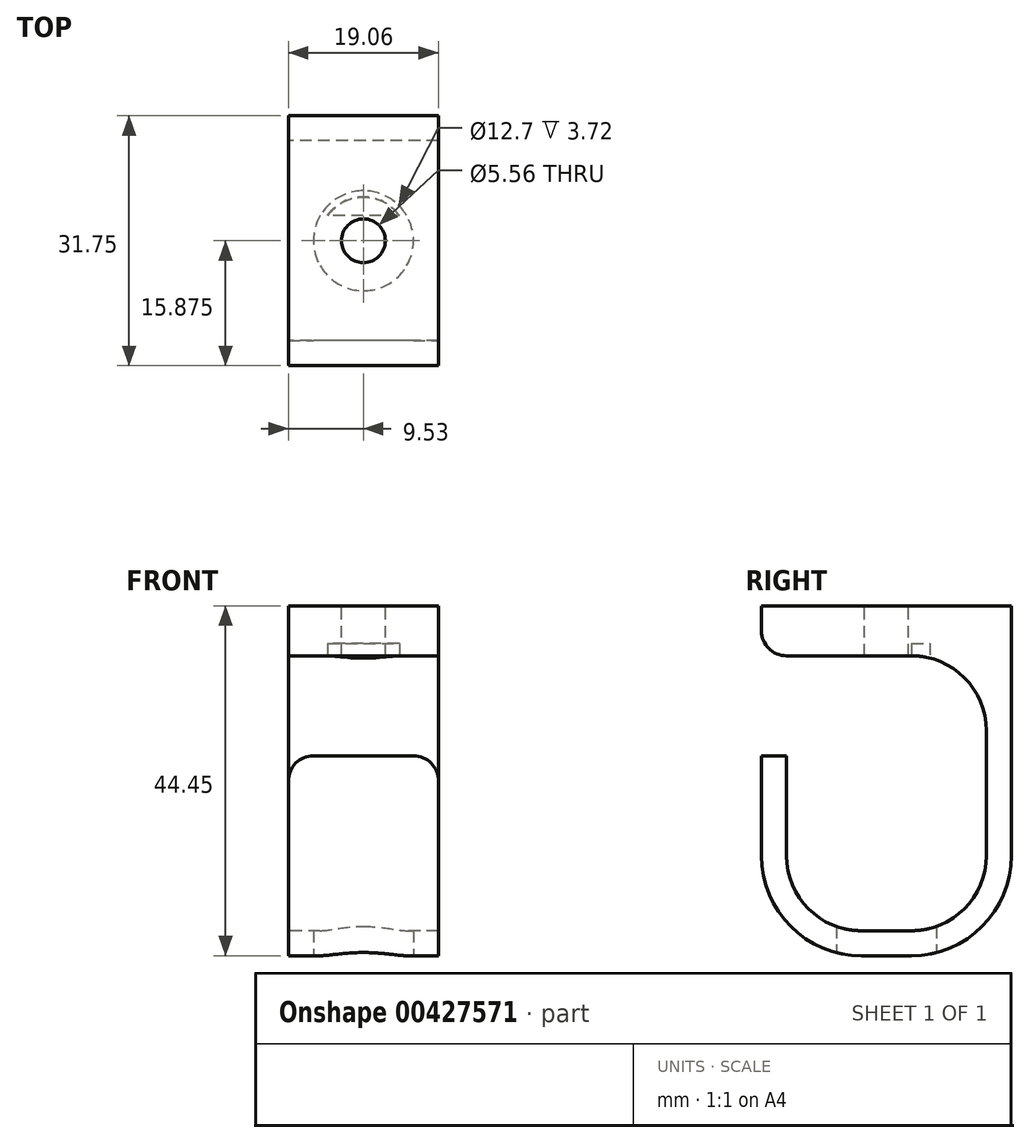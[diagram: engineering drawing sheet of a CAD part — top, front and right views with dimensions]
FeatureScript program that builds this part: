
annotation { "Feature Type Name" : "Feature", "Feature Type Description" : "" }
export const myFeature = defineFeature(function(context is Context, id is Id, definition is map)
    precondition{}
    {
        {
            var Q0;
            Q0=qCreatedBy(makeId("Right.planeOp"),FACE);
            var sketch = newSketch(context, id + "F0", { "sketchPlane" : qUnion([Q0])});
            skLineSegment(sketch, "E0.bottom", {"start": v(0, 44.45) * mm, "end": v(31.75, 44.45) * mm});
            skLineSegment(sketch, "E0.top", {"start": v(0, 0) * mm, "end": v(31.75, 0) * mm});
            skLineSegment(sketch, "E0.left", {"start": v(0, 44.45) * mm, "end": v(0, 0) * mm});
            skLineSegment(sketch, "E0.right", {"start": v(31.75, 44.45) * mm, "end": v(31.75, 0) * mm});
            skLineSegment(sketch, "E1", {"start": v(0, 38.1) * mm, "end": v(28.58, 38.1) * mm});
            skLineSegment(sketch, "E2", {"start": v(28.58, 38.1) * mm, "end": v(28.58, 0) * mm});
            skLineSegment(sketch, "E3", {"start": v(31.75, 3.18) * mm, "end": v(0, 3.17) * mm});
            skLineSegment(sketch, "E4", {"start": v(3.17, 44.45) * mm, "end": v(3.17, 0) * mm});
            skLineSegment(sketch, "E5", {"start": v(0, 12.7) * mm, "end": v(31.75, 12.7) * mm, "construction": true});
            skLineSegment(sketch, "E6", {"start": v(12.7, 0) * mm, "end": v(12.7, 44.45) * mm, "construction": true});
            skLineSegment(sketch, "E7", {"start": v(19.05, 44.45) * mm, "end": v(19.05, 0) * mm, "construction": true});
            skArc(sketch, "E8", {"start": v(3.17, 12.7) * mm, "mid": v(5.96, 5.96) * mm, "end": v(12.7, 3.17) * mm});
            skArc(sketch, "E9", {"start": v(19.05, 3.17) * mm, "mid": v(25.79, 5.96) * mm, "end": v(28.58, 12.7) * mm});
            skLineSegment(sketch, "E10", {"start": v(0, 28.57) * mm, "end": v(31.75, 28.58) * mm, "construction": true});
            skArc(sketch, "E11", {"start": v(28.58, 28.58) * mm, "mid": v(25.79, 35.31) * mm, "end": v(19.05, 38.1) * mm});
            skLineSegment(sketch, "E12", {"start": v(0, 25.4) * mm, "end": v(31.75, 25.4) * mm, "construction": true});
            skArc(sketch, "E13", {"start": v(0, 12.7) * mm, "mid": v(3.72, 3.72) * mm, "end": v(12.7, 0) * mm});
            skArc(sketch, "E14", {"start": v(19.05, 0) * mm, "mid": v(28.03, 3.72) * mm, "end": v(31.75, 12.7) * mm});
            skLineSegment(sketch, "E15", {"start": v(0, 25.4) * mm, "end": v(3.17, 25.4) * mm});
            skSolve(sketch);
        }
        {
            var Q0;
            {var subQ5=sQuery(id+"F0.wireOp",EDGE,"E0.right");var subQ6=sQuery(id+"F0.wireOp",EDGE,"E0.bottom");var subQ7=makeQuery(id+"F0.imprint","INTERSECT",VERTEX,{"derivedFrom":[subQ6,subQ5]});Q0=makeQuery(id+"F0.imprint","IMPRINT",FACE,{"disambiguationData":[TD([[makeQuery(id+"F0.imprint","IMPRINT",EDGE,{"disambiguationData":[TD([[subQ7,1.0]])],"derivedFrom":subQ6}),-1.0]])]});}
            var Q1;
            {var subQ0=sQuery(id+"F0.wireOp",EDGE,"E0.left");var subQ1=sQuery(id+"F0.wireOp",EDGE,"E0.bottom");var subQ2=makeQuery(id+"F0.imprint","INTERSECT",VERTEX,{"derivedFrom":[subQ1,subQ0]});Q1=makeQuery(id+"F0.imprint","IMPRINT",FACE,{"disambiguationData":[TD([[makeQuery(id+"F0.imprint","IMPRINT",EDGE,{"disambiguationData":[TD([[subQ2,-1.0]])],"derivedFrom":subQ1}),-1.0]])]});}
            var Q2;
            {var subQ3=sQuery(id+"F0.wireOp",EDGE,"E11");Q2=makeQuery(id+"F0.imprint","IMPRINT",FACE,{"disambiguationData":[TD([[makeQuery(id+"F0.imprint","IMPRINT",EDGE,{"derivedFrom":subQ3}),-1.0]])]});}
            var Q3;
            {var subQ0=sQuery(id+"F0.wireOp",EDGE,"E9");Q3=makeQuery(id+"F0.imprint","IMPRINT",FACE,{"disambiguationData":[TD([[makeQuery(id+"F0.imprint","IMPRINT",EDGE,{"derivedFrom":subQ0}),-1.0]])]});}
            var Q4;
            {var subQ2=sQuery(id+"F0.wireOp",EDGE,"E13");var subQ5=sQuery(id+"F0.wireOp",EDGE,"E0.top");var subQ6=makeQuery(id+"F0.imprint","INTERSECT",VERTEX,{"derivedFrom":[subQ5,subQ2]});Q4=makeQuery(id+"F0.imprint","IMPRINT",FACE,{"disambiguationData":[TD([[makeQuery(id+"F0.imprint","IMPRINT",EDGE,{"disambiguationData":[TD([[subQ6,-1.0]])],"derivedFrom":subQ5}),1.0]])]});}
            var Q5;
            {var subQ0=sQuery(id+"F0.wireOp",EDGE,"E8");Q5=makeQuery(id+"F0.imprint","IMPRINT",FACE,{"disambiguationData":[TD([[makeQuery(id+"F0.imprint","IMPRINT",EDGE,{"derivedFrom":subQ0}),-1.0]])]});}
            var Q6;
            {var subQ4=sQuery(id+"F0.wireOp",EDGE,"UCciuxyD-qlXf-moOq-a4FD-n2S9QXWjRClS");Q6=makeQuery(id+"F0.imprint","IMPRINT",FACE,{"disambiguationData":[TD([[makeQuery(id+"F0.imprint","IMPRINT",EDGE,{"derivedFrom":subQ4}),1.0]])]});}
            var Q7;
            {var subQ4=sQuery(id+"F0.wireOp",EDGE,"E15");Q7=makeQuery(id+"F0.imprint","IMPRINT",FACE,{"disambiguationData":[TD([[makeQuery(id+"F0.imprint","IMPRINT",EDGE,{"derivedFrom":subQ4}),-1.0]])]});}
            extrude(context, id + "F1", {"entities" : qUnion([Q0, Q1, Q2, Q3, Q4, Q5, Q6, Q7]), "endBound" : BoundingType.SYMMETRIC, "depth" : 19.05 * mm});
        }
        {
            var Q0;
            Q0=makeQuery(id+"F1.opExtrude","SWEPT_FACE",FACE,{"disambiguationData":[OSD([sQuery(id+"F0.wireOp",EDGE,"E0.top")])]});
            var sketch = newSketch(context, id + "F2", { "sketchPlane" : qUnion([Q0])});
            skLineSegment(sketch, "E16", {"start": v(0, -12.7) * mm, "end": v(0, -19.05) * mm, "construction": true});
            skLineSegment(sketch, "E17", {"start": v(9.53, -15.88) * mm, "end": v(-9.53, -15.88) * mm, "construction": true});
            skLineSegment(sketch, "E18.bottom", {"start": v(6.35, -22.23) * mm, "end": v(-6.35, -22.23) * mm});
            skLineSegment(sketch, "E18.top", {"start": v(6.35, -9.52) * mm, "end": v(-6.35, -9.52) * mm});
            skLineSegment(sketch, "E18.left", {"start": v(6.35, -22.23) * mm, "end": v(6.35, -9.53) * mm});
            skLineSegment(sketch, "E18.right", {"start": v(-6.35, -22.23) * mm, "end": v(-6.35, -9.53) * mm});
            skPoint(sketch, "E18.middle", {"position": v(0, -15.87) * mm});
            skSolve(sketch);
        }
        {
            var Q0;
            {var subQ0=sQuery(id+"F2.wireOp",EDGE,"E18.left");var subQ1=sQuery(id+"F0.wireOp",EDGE,"E0.top");var subQ2=makeQuery(id+"F1.opExtrude","SWEPT_EDGE",EDGE,{"disambiguationData":[OSD([subQ1,sQuery(id+"F0.wireOp",EDGE,"E14")])]});var subQ3=makeQuery(id+"F2.imprint","INTERSECT",VERTEX,{"derivedFrom":[subQ2,subQ0]});Q0=makeQuery(id+"F2.imprint","IMPRINT",FACE,{"disambiguationData":[TD([[makeQuery(id+"F2.imprint","IMPRINT",EDGE,{"disambiguationData":[TD([[subQ3,-1.0]])],"derivedFrom":subQ0}),1.0]])]});}
            var Q1;
            {var subQ0=sQuery(id+"F2.wireOp",EDGE,"E18.top");Q1=makeQuery(id+"F2.imprint","IMPRINT",FACE,{"disambiguationData":[TD([[makeQuery(id+"F2.imprint","IMPRINT",EDGE,{"derivedFrom":subQ0}),1.0]])]});}
            var Q2;
            {var subQ0=sQuery(id+"F2.wireOp",EDGE,"E18.bottom");Q2=makeQuery(id+"F2.imprint","IMPRINT",FACE,{"disambiguationData":[TD([[makeQuery(id+"F2.imprint","IMPRINT",EDGE,{"derivedFrom":subQ0}),-1.0]])]});}
            extrude(context, id + "F3", {"entities" : qUnion([Q0, Q1, Q2]), "operationType" : NewBodyOperationType.REMOVE, "endBound" : BoundingType.UP_TO_NEXT, "oppositeDirection" : true, "depth" : 25.4 * mm});
        }
        {
            var Q0;
            Q0=makeQuery(id+"F3.boolean.opBoolean","COPY",EDGE,{"derivedFrom":makeQuery(id+"F3.opExtrude","SWEPT_EDGE",EDGE,{"disambiguationData":[OSD([sQuery(id+"F2.wireOp",EDGE,"E18.bottom"),sQuery(id+"F2.wireOp",EDGE,"E18.right")])]})});
            var Q1;
            Q1=makeQuery(id+"F3.boolean.opBoolean","COPY",EDGE,{"derivedFrom":makeQuery(id+"F3.opExtrude","SWEPT_EDGE",EDGE,{"disambiguationData":[OSD([sQuery(id+"F2.wireOp",EDGE,"E18.top"),sQuery(id+"F2.wireOp",EDGE,"E18.right")])]})});
            var Q2;
            Q2=makeQuery(id+"F3.boolean.opBoolean","COPY",EDGE,{"derivedFrom":makeQuery(id+"F3.opExtrude","SWEPT_EDGE",EDGE,{"disambiguationData":[OSD([sQuery(id+"F2.wireOp",EDGE,"E18.top"),sQuery(id+"F2.wireOp",EDGE,"E18.left")])]})});
            var Q3;
            Q3=makeQuery(id+"F3.boolean.opBoolean","COPY",EDGE,{"derivedFrom":makeQuery(id+"F3.opExtrude","SWEPT_EDGE",EDGE,{"disambiguationData":[OSD([sQuery(id+"F2.wireOp",EDGE,"E18.bottom"),sQuery(id+"F2.wireOp",EDGE,"E18.left")])]})});
            fillet(context, id + "F4", {"entities" : qUnion([Q0, Q1, Q2, Q3]), "radius" : 6.35 * mm, "tangentPropagation" : true, "allowEdgeOverflow" : false});
        }
        {
            var Q0;
            Q0=makeQuery(id+"F1.opExtrude","CAP_EDGE",EDGE,{"disambiguationData":[OSD([sQuery(id+"F0.wireOp",EDGE,"UCciuxyD-qlXf-moOq-a4FD-n2S9QXWjRClS")])],"isStart":false});
            var Q1;
            Q1=makeQuery(id+"F1.opExtrude","CAP_EDGE",EDGE,{"disambiguationData":[OSD([sQuery(id+"F0.wireOp",EDGE,"UCciuxyD-qlXf-moOq-a4FD-n2S9QXWjRClS")])],"isStart":true});
            var Q2;
            Q2=makeQuery(id+"F1.opExtrude","SWEPT_EDGE",EDGE,{"disambiguationData":[OSD([sQuery(id+"F0.wireOp",EDGE,"E0.left"),sQuery(id+"F0.wireOp",EDGE,"E1")])]});
            var Q3;
            Q3=makeQuery(id+"F1.opExtrude","CAP_EDGE",EDGE,{"disambiguationData":[OSD([sQuery(id+"F0.wireOp",EDGE,"E15")])],"isStart":false});
            var Q4;
            Q4=makeQuery(id+"F1.opExtrude","CAP_EDGE",EDGE,{"disambiguationData":[OSD([sQuery(id+"F0.wireOp",EDGE,"E15")])],"isStart":true});
            fillet(context, id + "F5", {"entities" : qUnion([Q0, Q1, Q2, Q3, Q4]), "radius" : 3.17 * mm, "tangentPropagation" : true, "allowEdgeOverflow" : false});
        }
        {
            var Q0;
            Q0=makeQuery(id+"F1.opExtrude","SWEPT_FACE",FACE,{"disambiguationData":[OSD([sQuery(id+"F0.wireOp",EDGE,"E0.bottom")])]});
            var sketch = newSketch(context, id + "F6", { "sketchPlane" : qUnion([Q0])});
            skLineSegment(sketch, "E19", {"start": v(0, 31.75) * mm, "end": v(0, 0) * mm, "construction": true});
            skLineSegment(sketch, "E20", {"start": v(9.53, 15.88) * mm, "end": v(-9.53, 15.88) * mm, "construction": true});
            skCircle(sketch, "E21", {"center": v(0, 15.88) * mm, "radius": 2.78 * mm});
            skSolve(sketch);
        }
        {
            var Q0;
            Q0=makeQuery(id+"F6.imprint","IMPRINT",FACE,{"disambiguationData":[TD([[makeQuery(id+"F6.imprint","IMPRINT",EDGE,{"derivedFrom":sQuery(id+"F6.wireOp",EDGE,"E21")}),1.0]])]});
            extrude(context, id + "F7", {"entities" : qUnion([Q0]), "operationType" : NewBodyOperationType.REMOVE, "endBound" : BoundingType.UP_TO_NEXT, "oppositeDirection" : true, "depth" : 25.4 * mm});
        }
        {
            var Q0;
            Q0=makeQuery(id+"F1.opExtrude","SWEPT_FACE",FACE,{"disambiguationData":[OSD([sQuery(id+"F0.wireOp",EDGE,"E1")])]});
            var sketch = newSketch(context, id + "F8", { "sketchPlane" : qUnion([Q0])});
            skCircle(sketch, "E22", {"center": v(0, -15.88) * mm, "radius": 5.56 * mm});
            skSolve(sketch);
        }
        {
            var Q0;
            {var subQ10=sQuery(id+"F0.wireOp",EDGE,"E1");var subQ15=makeQuery(id+"F1.opExtrude","SWEPT_FACE",FACE,{"disambiguationData":[OSD([subQ10])]});var subQ17=sQuery(id+"F6.wireOp",EDGE,"E21");var subQ24=makeQuery(id+"F7.boolean.opBoolean","COPY",EDGE,{"derivedFrom":makeQuery(id+"F7.opExtrude","TWEAK_EDGE",EDGE,{"derivedFrom":[subQ15,makeQuery(id+"F6.imprint","IMPRINT",EDGE,{"derivedFrom":subQ17})]})});Q0=makeQuery(id+"F8.imprint","IMPRINT",FACE,{"disambiguationData":[TD([[makeQuery(id+"F8.imprint","IMPRINT",EDGE,{"derivedFrom":subQ24}),-1.0]])]});}
            var Q1;
            {var subQ0=sQuery(id+"F8.wireOp",EDGE,"E22");var subQ1=sQuery(id+"F0.wireOp",EDGE,"E14");var subQ2=sQuery(id+"F0.wireOp",EDGE,"E13");var subQ3=sQuery(id+"F0.wireOp",EDGE,"UCciuxyD-qlXf-moOq-a4FD-n2S9QXWjRClS");var subQ4=sQuery(id+"F0.wireOp",EDGE,"E11");var subQ5=sQuery(id+"F0.wireOp",EDGE,"E9");var subQ6=sQuery(id+"F0.wireOp",EDGE,"E8");var subQ7=sQuery(id+"F0.wireOp",EDGE,"E4");var subQ8=sQuery(id+"F0.wireOp",EDGE,"E3");var subQ9=sQuery(id+"F0.wireOp",EDGE,"E2");var subQ10=sQuery(id+"F0.wireOp",EDGE,"E1");var subQ11=sQuery(id+"F0.wireOp",EDGE,"E0.right");var subQ12=sQuery(id+"F0.wireOp",EDGE,"E0.left");var subQ13=sQuery(id+"F0.wireOp",EDGE,"E0.top");var subQ14=sQuery(id+"F0.wireOp",EDGE,"E0.bottom");var subQ19=makeQuery(id+"F1.opExtrude","SWEPT_EDGE",EDGE,{"disambiguationData":[OSD([subQ10,subQ4])]});var subQ20=makeQuery(id+"F7.boolean.opBoolean","SPLIT",EDGE,{"disambiguationData":[TD([makeQuery(id+"F1.opExtrude","CAP_FACE",FACE,{"disambiguationData":[OSD([subQ14,subQ13,subQ12,subQ11,subQ10,subQ9,subQ8,subQ7,subQ6,subQ5,subQ4,subQ3,subQ2,subQ1])],"isStart":true})])],"derivedFrom":subQ19});var subQ21=makeQuery(id+"F8.imprint","INTERSECT",VERTEX,{"derivedFrom":[subQ20,subQ0]});Q1=makeQuery(id+"F8.imprint","IMPRINT",FACE,{"disambiguationData":[TD([[makeQuery(id+"F8.imprint","IMPRINT",EDGE,{"disambiguationData":[TD([[subQ21,-1.0]])],"derivedFrom":subQ0}),1.0]])]});}
            extrude(context, id + "F9", {"entities" : qUnion([Q0, Q1]), "operationType" : NewBodyOperationType.REMOVE, "endBound" : BoundingType.SYMMETRIC, "oppositeDirection" : true, "depth" : 3.17 * mm});
        }
    });
